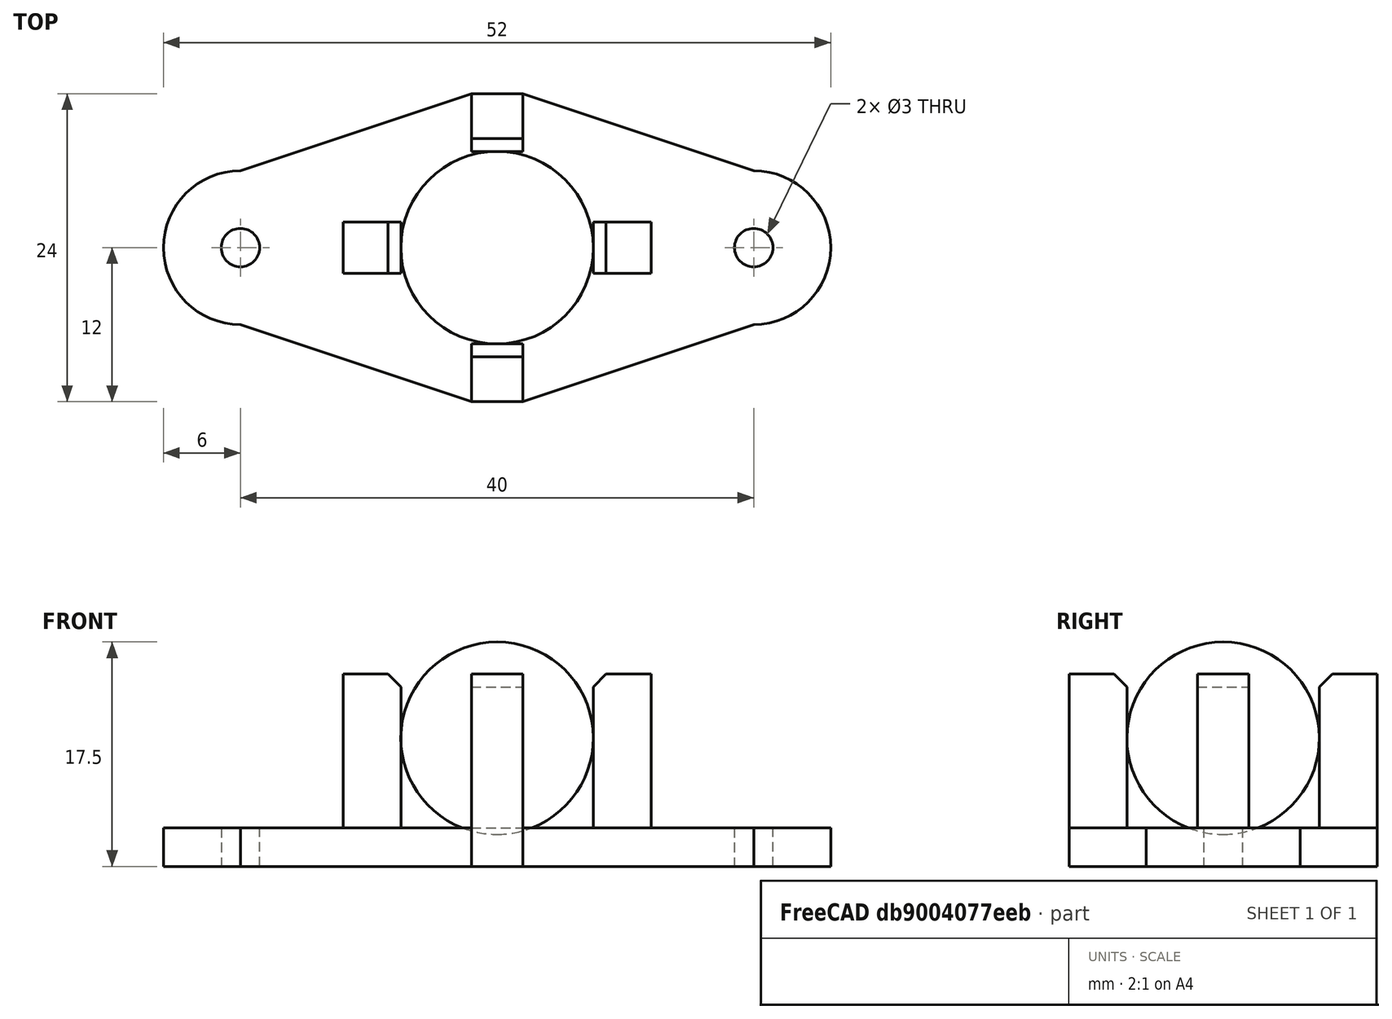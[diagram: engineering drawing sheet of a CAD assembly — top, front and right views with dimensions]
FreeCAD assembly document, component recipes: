
FREECAD ASSEMBLY — COMPONENT RECIPES ("Castor_W420_Steel_Ball")

This assembly document has 2 components, labeled P0..P1 below (a component is one placed body or linked part). 1 of them carries a construction recipe — the FreeCAD feature program that regenerates the part from scratch, quoted from this document or its linked companion documents; the rest are supplied as boundary geometry only. No exploded tour is included for this assembly.
COMPONENT P0 — recipe-attached ("Plastic_Bracket001", modeled in this document).
Construction recipe (the document's own serialized feature program — sketch geometry with constraints, then the solid features built on it; lengths are millimeters unless a unit is written):

FEATURE [Sketcher::SketchObject] Sketch
  ArcFitTolerance = 1e-06
  AttachmentSupport = -> [XY_Plane]
  FullyConstrained = false
  MakeInternals = false
  MapMode = 5
  sketch-geometry (10):
    g0: ArcOfCircle CenterX=20 CenterY=20 CenterZ=0 NormalX=0 NormalY=0 NormalZ=1 AngleXU=0 Radius=6 StartAngle=1.5708 EndAngle=4.71239
    g1: ArcOfCircle CenterX=60 CenterY=20 CenterZ=0 NormalX=0 NormalY=0 NormalZ=1 AngleXU=0 Radius=6 StartAngle=4.71239 EndAngle=7.85398
    g2: LineSegment StartX=20 StartY=26 StartZ=0 EndX=38 EndY=32 EndZ=0
    g3: LineSegment StartX=42 StartY=32 StartZ=0 EndX=60 EndY=26 EndZ=0
    g4: LineSegment StartX=20 StartY=14 StartZ=0 EndX=38 EndY=8 EndZ=0
    g5: LineSegment StartX=42 StartY=8 StartZ=0 EndX=60 EndY=14 EndZ=0
    g6: Circle CenterX=20 CenterY=20 CenterZ=0 NormalX=0 NormalY=0 NormalZ=1 AngleXU=0 Radius=1.5
    g7: Circle CenterX=60 CenterY=20 CenterZ=0 NormalX=0 NormalY=0 NormalZ=1 AngleXU=0 Radius=1.5
    g8: LineSegment StartX=38 StartY=32 StartZ=0 EndX=42 EndY=32 EndZ=0
    g9: LineSegment StartX=38 StartY=8 StartZ=0 EndX=42 EndY=8 EndZ=0
  constraints (19):
    c: Equal(g0,g1)
    c: Diameter(g0) = 12
    c: DistanceX(g0) = 20
    c: DistanceY(g0) = 20
    c: DistanceY(g5,g3) = 24
    c: Coincident(g2,g0)
    c: Coincident(g3,g1)
    c: Coincident(g4,g0)
    c: Coincident(g5,g1)
    c: Coincident(g6,g0)
    c: Coincident(g7,g1)
    c: Diameter(g6) = 3
    c: Equal(g6,g7)
    c: Coincident(g8,g2)
    c: Coincident(g8,g3)
    c: Horizontal(g8)
    c: Coincident(g9,g4)
    c: Coincident(g9,g5)
    c: Horizontal(g9)
FEATURE [PartDesign::Pad] Pad
  Direction = (0,0,1)
  Length = 3
  Length2 = 10
  Profile = -> Sketch
  ReferenceAxis = -> Sketch [N_Axis]
  Refine = true
  Suppressed = false
  Type = 0
FEATURE [Sketcher::SketchObject] Sketch001
  ArcFitTolerance = 1e-06
  AttachmentSupport = -> [Pad]
  FullyConstrained = true
  MakeInternals = false
  MapMode = 5
  Placement = pos=(0,0,3) rot=(0,0,1;0rad)
  sketch-geometry (16):
    g0: LineSegment StartX=38 StartY=32 StartZ=0 EndX=38 EndY=27.5 EndZ=0
    g1: LineSegment StartX=38 StartY=27.5 StartZ=0 EndX=42 EndY=27.5 EndZ=0
    g2: LineSegment StartX=42 StartY=27.5 StartZ=0 EndX=42 EndY=32 EndZ=0
    g3: LineSegment StartX=42 StartY=32 StartZ=0 EndX=38 EndY=32 EndZ=0
    g4: LineSegment StartX=38 StartY=12.5 StartZ=0 EndX=38 EndY=8 EndZ=0
    g5: LineSegment StartX=38 StartY=8 StartZ=0 EndX=42 EndY=8 EndZ=0
    g6: LineSegment StartX=42 StartY=8 StartZ=0 EndX=42 EndY=12.5 EndZ=0
    g7: LineSegment StartX=42 StartY=12.5 StartZ=0 EndX=38 EndY=12.5 EndZ=0
    g8: LineSegment StartX=28 StartY=22 StartZ=0 EndX=28 EndY=18 EndZ=0
    g9: LineSegment StartX=28 StartY=18 StartZ=0 EndX=32.5 EndY=18 EndZ=0
    g10: LineSegment StartX=32.5 StartY=18 StartZ=0 EndX=32.5 EndY=22 EndZ=0
    g11: LineSegment StartX=32.5 StartY=22 StartZ=0 EndX=28 EndY=22 EndZ=0
    g12: LineSegment StartX=47.5 StartY=22 StartZ=0 EndX=47.5 EndY=18 EndZ=0
    g13: LineSegment StartX=47.5 StartY=18 StartZ=0 EndX=52 EndY=18 EndZ=0
    g14: LineSegment StartX=52 StartY=18 StartZ=0 EndX=52 EndY=22 EndZ=0
    g15: LineSegment StartX=52 StartY=22 StartZ=0 EndX=47.5 EndY=22 EndZ=0
  constraints (48):
    c: Coincident(g0,g1)
    c: Coincident(g1,g2)
    c: Coincident(g2,g3)
    c: Coincident(g3,g0)
    c: Vertical(g0)
    c: Vertical(g2)
    c: Horizontal(g1)
    c: Horizontal(g3)
    c: Coincident(g4,g5)
    c: Coincident(g5,g6)
    c: Coincident(g6,g7)
    c: Coincident(g7,g4)
    c: Vertical(g4)
    c: Vertical(g6)
    c: Horizontal(g5)
    c: Horizontal(g7)
    c: Coincident(g8,g9)
    c: Coincident(g9,g10)
    c: Coincident(g10,g11)
    c: Coincident(g11,g8)
    c: Vertical(g8)
    c: Vertical(g10)
    c: Horizontal(g9)
    c: Horizontal(g11)
    c: Coincident(g12,g13)
    c: Coincident(g13,g14)
    c: Coincident(g14,g15)
    c: Coincident(g15,g12)
    c: Vertical(g12)
    c: Vertical(g14)
    c: Horizontal(g13)
    c: Horizontal(g15)
    c: DistanceX(g3,g3) = 4
    c: Equal(g3,g7)
    c: DistanceY(g8,g8) = 4
    c: Equal(g8,g14)
    c: DistanceY(g2,g2) = 4.5
    c: Equal(g2,g6)
    c: DistanceX(g11,g11) = 4.5
    c: Equal(g11,g15)
    c: DistanceX(g4) = 38
    c: DistanceY(g4) = 8
    c: DistanceX(g0) = 38
    c: DistanceY(g0) = 32
    c: DistanceX(g9) = 32.5
    c: DistanceY(g9) = 18
    c: DistanceX(g12) = 47.5
    c: DistanceY(g12) = 18
FEATURE [PartDesign::Pad] Pad001
  BaseFeature = -> Pad
  Direction = (0,0,1)
  Length = 12
  Length2 = 10
  Profile = -> Sketch001
  ReferenceAxis = -> Sketch001 [N_Axis]
  Refine = true
  Suppressed = false
  Type = 0
FEATURE [PartDesign::Chamfer] Chamfer
  Angle = 45
  Base = -> Pad001 [Edge63,Edge54,Edge47,Edge67]
  BaseFeature = -> Pad001
  ChamferType = 0
  FlipDirection = false
  Refine = true
  Size = 1
  Size2 = 1
  SupportTransform = false
  Suppressed = false
  UseAllEdges = false
FEATURE [PartDesign::Body] Body  label="Plastic_Bracket"
  AllowCompound = false
  Group = -> [Sketch,Pad,Sketch001,Pad001,Chamfer]
  Origin = -> Origin
  Tip = -> Chamfer
COMPONENT P1 — geometry summary ("Steel_Ball001"; no construction recipe available for this part):
  bounding box: 15.0 x 15.0 x 15.0 mm
  tessellated surface: 8,000 triangles
  volume: 1767 mm^3 (52% of its bounding box)
  symmetry: revolution-symmetric about the x axis through its bounding-box center; revolution-symmetric about the y axis through its bounding-box center; revolution-symmetric about the z axis through its bounding-box center; mirror-symmetric across its x mid-plane, y mid-plane, z mid-plane
PROVENANCE & LICENSES
A FreeCAD (.FCStd) document from a public repository crawl; recipes are the document's own serialized feature recipes (and, for linked parts, companion documents' recipes).
License: mit.
